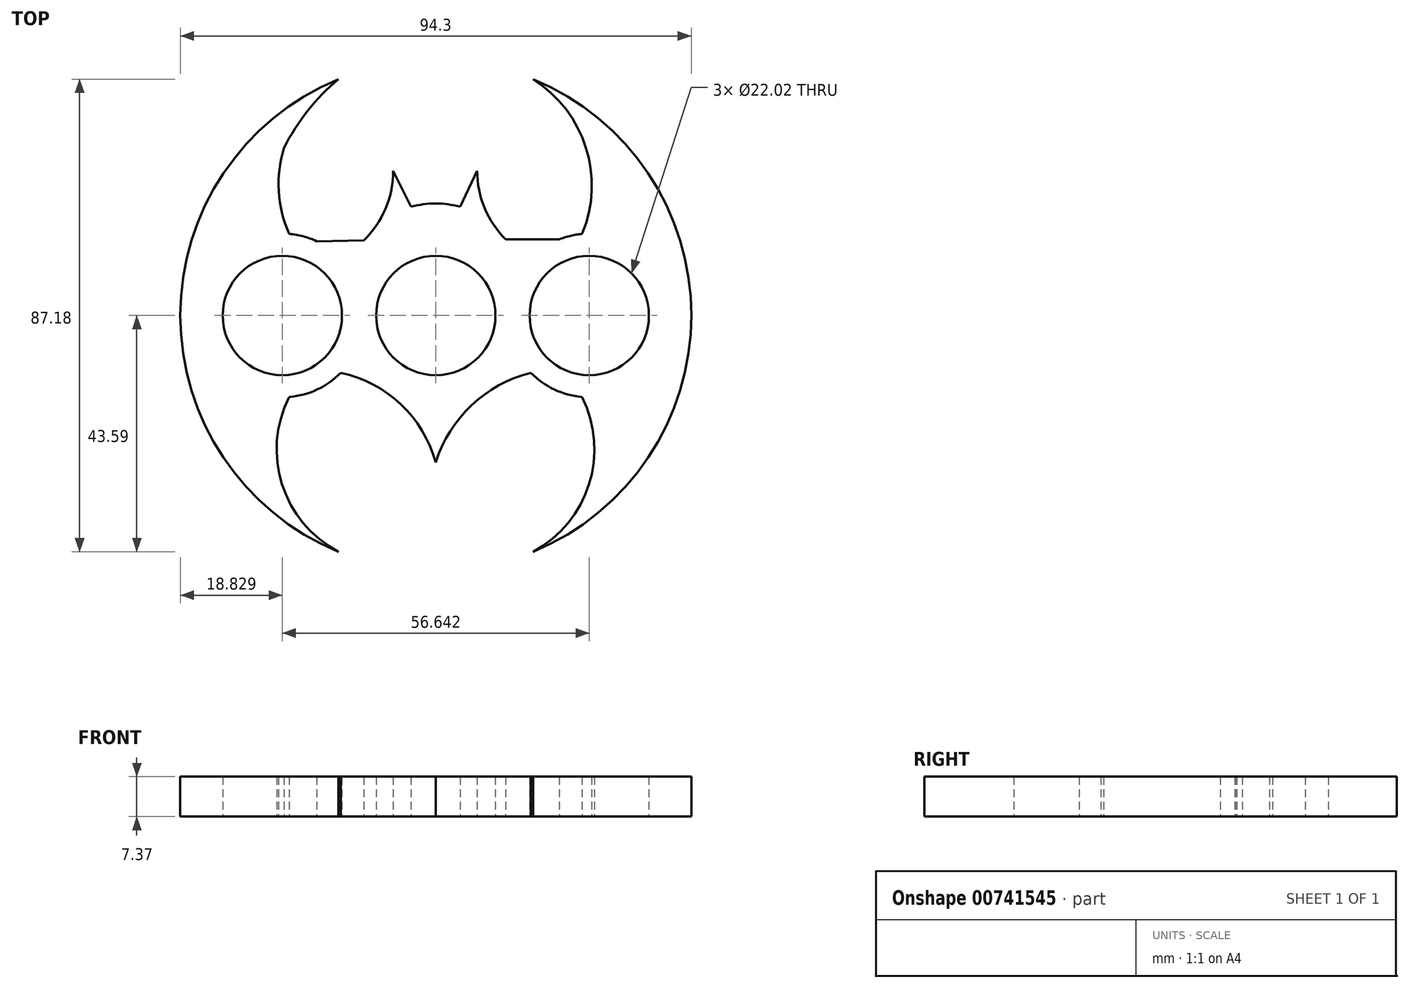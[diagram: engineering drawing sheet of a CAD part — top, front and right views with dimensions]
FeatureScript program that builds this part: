
annotation { "Feature Type Name" : "Feature", "Feature Type Description" : "" }
export const myFeature = defineFeature(function(context is Context, id is Id, definition is map)
    precondition{}
    {
        {
            var Q0;
            Q0=qCreatedBy(makeId("Top.planeOp"),FACE);
            var sketch = newSketch(context, id + "F0", { "sketchPlane" : qUnion([Q0])});
            skCircle(sketch, "E0", {"center": v(0, 0) * mm, "radius": 11.01 * mm});
            skCircle(sketch, "E1", {"center": v(28.32, 0) * mm, "radius": 11.01 * mm});
            skCircle(sketch, "E2", {"center": v(-28.32, 0) * mm, "radius": 11.01 * mm});
            skPoint(sketch, "E3.orphan", {"position": v(-40.62, -26.49) * mm});
            skPoint(sketch, "E4.orphan", {"position": v(37.86, -26.49) * mm});
            skPoint(sketch, "E5.orphan", {"position": v(38.57, 26.34) * mm});
            skPoint(sketch, "E6.orphan", {"position": v(-42.26, 26.34) * mm});
            skPoint(sketch, "E7.end.orphan", {"position": v(6.35, 34.78) * mm});
            skPoint(sketch, "E8.end.orphan", {"position": v(-7.47, 34.78) * mm});
            skPoint(sketch, "E9.trimOffspring.end.orphan", {"position": v(24.19, 20.43) * mm});
            skPoint(sketch, "E10.end.orphan", {"position": v(40.56, -16.87) * mm});
            skPoint(sketch, "E11.start.orphan", {"position": v(5.97, -12.84) * mm});
            skPoint(sketch, "E12.trimOffspring.end.orphan", {"position": v(-5.97, -12.84) * mm});
            skPoint(sketch, "E13.start.orphan", {"position": v(-1.73, -25.43) * mm});
            skPoint(sketch, "E14.end.orphan", {"position": v(2.02, -25.43) * mm});
            skPoint(sketch, "E14.start.orphan", {"position": v(0, -29.42) * mm});
            skPoint(sketch, "E15.start.orphan", {"position": v(-40.55, -16.87) * mm});
            skPoint(sketch, "E16.start.orphan", {"position": v(-24.21, 20.43) * mm});
            skArc(sketch, "E17", {"start": v(-21.97, 13.7) * mm, "mid": v(-24.46, 14.6) * mm, "end": v(-27.06, 15.04) * mm});
            skArc(sketch, "E18", {"start": v(17.53, -10.56) * mm, "mid": v(21.87, -13.65) * mm, "end": v(27.01, -15.04) * mm});
            skArc(sketch, "E19.trimOffspring", {"start": v(7.92, 12.86) * mm, "mid": v(7.78, 12.94) * mm, "end": v(7.63, 13.03) * mm});
            skArc(sketch, "E20", {"start": v(-17.99, 43.59) * mm, "mid": v(-47.15, 0) * mm, "end": v(-17.99, -43.59) * mm});
            skArc(sketch, "E21", {"start": v(-17.99, 43.59) * mm, "mid": v(-23.62, 37.78) * mm, "end": v(-27.99, 30.96) * mm});
            skLineSegment(sketch, "E22", {"start": v(-21.97, 13.7) * mm, "end": v(-13.28, 13.88) * mm});
            skLineSegment(sketch, "E23", {"start": v(12.89, 14.06) * mm, "end": v(22.8, 14.06) * mm});
            skLineSegment(sketch, "E24", {"start": v(-5.28, 14.06) * mm, "end": v(-5.26, 14.15) * mm});
            skPoint(sketch, "E25.endSnap0", {"position": v(0, 15.1) * mm});
            skLineSegment(sketch, "E26", {"start": v(7.96, 12.76) * mm, "end": v(7.92, 12.86) * mm});
            skPoint(sketch, "E27.orphan", {"position": v(5.52, 14.06) * mm});
            skLineSegment(sketch, "E28.trimOffspring", {"start": v(-5.53, 14.05) * mm, "end": v(-5.28, 14.06) * mm});
            skPoint(sketch, "E29.end.orphan", {"position": v(0, 18.36) * mm});
            skPoint(sketch, "E30.end.orphan", {"position": v(-2.71, 26.44) * mm});
            skPoint(sketch, "E31.trimOffspring.end.orphan", {"position": v(2.3, 26.44) * mm});
            skLineSegment(sketch, "E32", {"start": v(-7.85, 26.68) * mm, "end": v(-4.57, 20.06) * mm});
            skPoint(sketch, "E33.end.orphan", {"position": v(7.48, 26.68) * mm});
            skLineSegment(sketch, "E34", {"start": v(4.5, 20.06) * mm, "end": v(7.63, 26.68) * mm});
            skArc(sketch, "E35", {"start": v(4.5, 20.06) * mm, "mid": v(-0.03, 20.68) * mm, "end": v(-4.57, 20.06) * mm});
            skArc(sketch, "E36", {"start": v(27.01, 15.04) * mm, "mid": v(27.72, 30.97) * mm, "end": v(17.99, 43.59) * mm});
            skPoint(sketch, "E37.orphan", {"position": v(32.31, 14.56) * mm});
            skArc(sketch, "E38", {"start": v(-27.99, 30.96) * mm, "mid": v(-28.98, 22.92) * mm, "end": v(-27.06, 15.04) * mm});
            skPoint(sketch, "E39.orphan", {"position": v(-32.3, 14.56) * mm});
            skArc(sketch, "E40.trimOffspring", {"start": v(17.99, -43.59) * mm, "mid": v(47.15, 0) * mm, "end": v(17.99, 43.59) * mm});
            skLineSegment(sketch, "E41", {"start": v(0, -27.1) * mm, "end": v(0, -21.96) * mm});
            skArc(sketch, "E42", {"start": v(0, -27.1) * mm, "mid": v(-6.46, -16.39) * mm, "end": v(-17.53, -10.56) * mm});
            skArc(sketch, "E43", {"start": v(17.53, -10.56) * mm, "mid": v(6.61, -16.55) * mm, "end": v(0, -27.1) * mm});
            skArc(sketch, "E44", {"start": v(17.99, -43.59) * mm, "mid": v(28.28, -31.15) * mm, "end": v(27.01, -15.04) * mm});
            skPoint(sketch, "E45.orphan", {"position": v(32.31, -14.56) * mm});
            skArc(sketch, "E46", {"start": v(-27.06, -15.04) * mm, "mid": v(-28.36, -31.17) * mm, "end": v(-17.99, -43.59) * mm});
            skPoint(sketch, "E47.orphan", {"position": v(-32.3, -14.56) * mm});
            skArc(sketch, "E48", {"start": v(7.63, 26.68) * mm, "mid": v(9, 19.85) * mm, "end": v(12.89, 14.06) * mm});
            skArc(sketch, "E49", {"start": v(-13.28, 13.88) * mm, "mid": v(-9.27, 19.73) * mm, "end": v(-7.85, 26.68) * mm});
            skPoint(sketch, "E50.start.orphan", {"position": v(7.63, 13.03) * mm});
            skPoint(sketch, "E51.orphan", {"position": v(7.63, 14.06) * mm});
            skPoint(sketch, "E52.start.orphan", {"position": v(-7.85, 12.9) * mm});
            skPoint(sketch, "E53.orphan", {"position": v(-7.85, 14) * mm});
            skArc(sketch, "E54.trimOffspring", {"start": v(-27.06, -15.04) * mm, "mid": v(-21.9, -13.66) * mm, "end": v(-17.53, -10.56) * mm});
            skArc(sketch, "E55.trimOffspring", {"start": v(27.01, 15.04) * mm, "mid": v(24.87, 14.7) * mm, "end": v(22.8, 14.06) * mm});
            skSolve(sketch);
        }
        {
            var Q0;
            Q0 = qSketchRegion(id + "F0", true);
            extrude(context, id + "F1", {"entities" : qUnion([Q0]), "depth" : 7.37 * mm, "offsetDistance" : 25.4 * mm});
        }
    });
